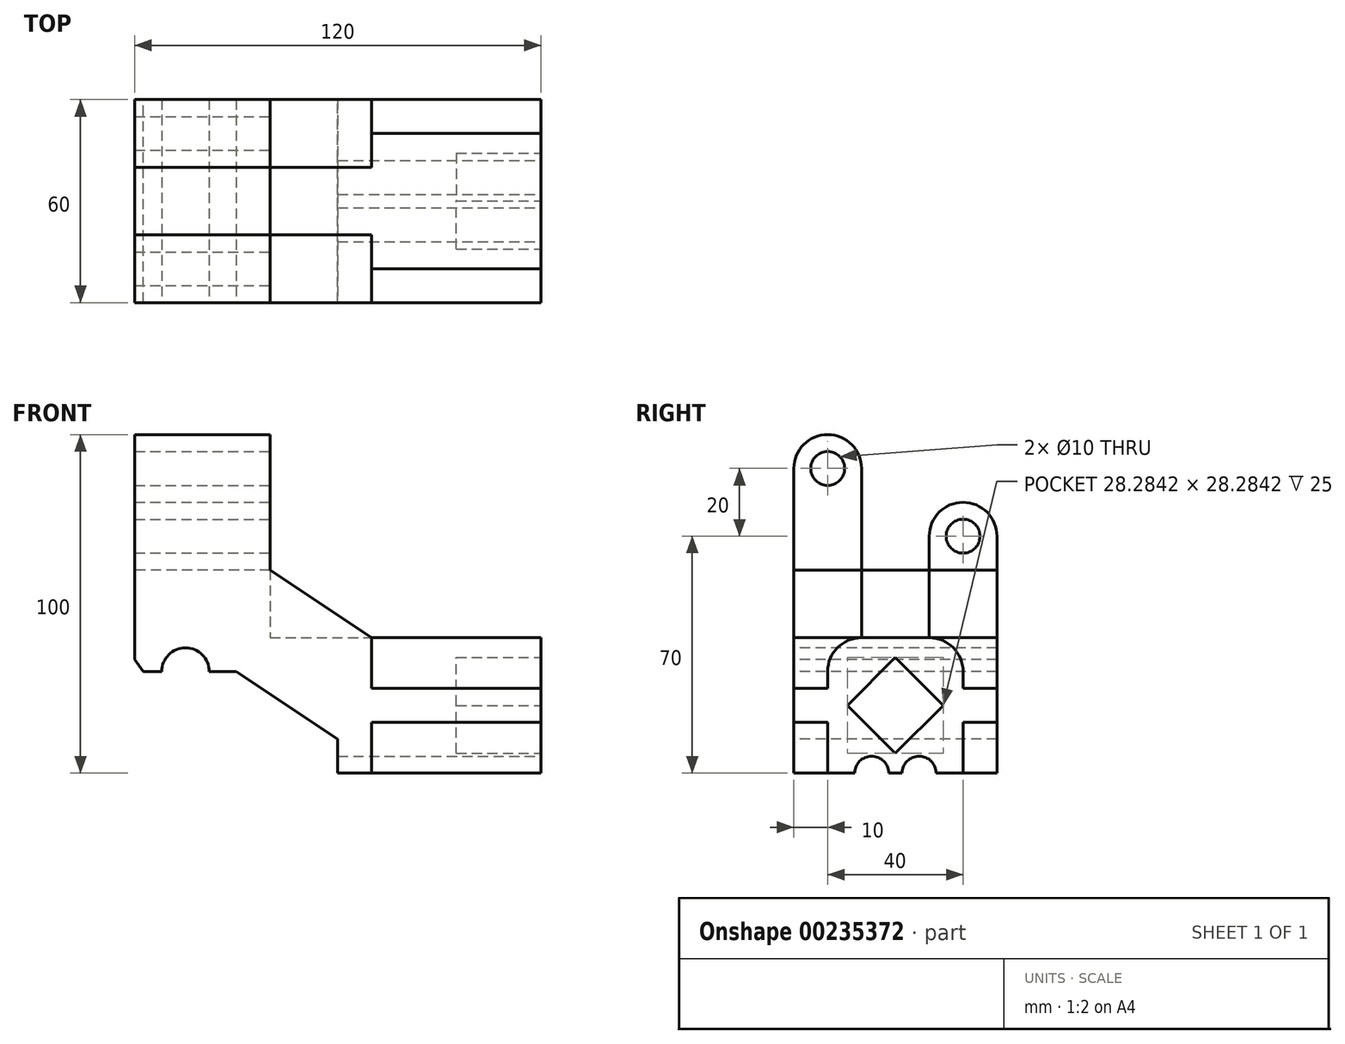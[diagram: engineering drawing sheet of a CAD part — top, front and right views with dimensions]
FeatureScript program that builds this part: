
annotation { "Feature Type Name" : "Feature", "Feature Type Description" : "" }
export const myFeature = defineFeature(function(context is Context, id is Id, definition is map)
    precondition{}
    {
        {
            var Q0;
            Q0=qCreatedBy(makeId("Front.planeOp"),FACE);
            var sketch = newSketch(context, id + "F0", { "sketchPlane" : qUnion([Q0])});
            skLineSegment(sketch, "E0", {"start": v(-120, 40) * mm, "end": v(-80, 40) * mm});
            skLineSegment(sketch, "E1", {"start": v(-80, 40) * mm, "end": v(-50, 20) * mm});
            skLineSegment(sketch, "E2", {"start": v(-50, 20) * mm, "end": v(-50, -20) * mm});
            skLineSegment(sketch, "E3", {"start": v(-50, -20) * mm, "end": v(-120, -20) * mm});
            skLineSegment(sketch, "E4", {"start": v(-120, -20) * mm, "end": v(-120, 40) * mm});
            skSolve(sketch);
        }
        {
            var Q0;
            Q0 = qSketchRegion(id + "F0", true);
            extrude(context, id + "F1", {"entities" : qUnion([Q0]), "depth" : 30 * mm, "hasSecondDirection" : true, "secondDirectionOppositeDirection" : true, "secondDirectionDepth" : 30 * mm});
        }
        {
            var Q0;
            Q0=makeQuery(id+"F1.opExtrude","CAP_FACE",FACE,{"disambiguationData":[OSD([sQuery(id+"F0.wireOp",EDGE,"E0"),sQuery(id+"F0.wireOp",EDGE,"E1"),sQuery(id+"F0.wireOp",EDGE,"E2"),sQuery(id+"F0.wireOp",EDGE,"E3"),sQuery(id+"F0.wireOp",EDGE,"E4")])],"isStart":false});
            var sketch = newSketch(context, id + "F2", { "sketchPlane" : qUnion([Q0])});
            skLineSegment(sketch, "E5", {"start": v(-128, 10) * mm, "end": v(-90, 10) * mm});
            skLineSegment(sketch, "E6", {"start": v(-90, 10) * mm, "end": v(-60, -10) * mm});
            skLineSegment(sketch, "E7", {"start": v(-60, -10) * mm, "end": v(-60, -28) * mm});
            skLineSegment(sketch, "E8", {"start": v(-60, -28) * mm, "end": v(-128, -28) * mm});
            skLineSegment(sketch, "E9", {"start": v(-128, -28) * mm, "end": v(-128, 10) * mm});
            skSolve(sketch);
        }
        {
            var Q0;
            Q0=makeQuery(id+"F1.opExtrude","SWEPT_FACE",FACE,{"disambiguationData":[OSD([sQuery(id+"F0.wireOp",EDGE,"E2")])]});
            var sketch = newSketch(context, id + "F3", { "sketchPlane" : qUnion([Q0])});
            skLineSegment(sketch, "E10.bottom", {"start": v(10, 48) * mm, "end": v(-10, 48) * mm});
            skLineSegment(sketch, "E10.top", {"start": v(10, -48) * mm, "end": v(-10, -48) * mm});
            skLineSegment(sketch, "E10.left", {"start": v(10, 48) * mm, "end": v(10, -48) * mm});
            skLineSegment(sketch, "E10.right", {"start": v(-10, 48) * mm, "end": v(-10, -48) * mm});
            skPoint(sketch, "E10.middle", {"position": v(0, 0) * mm});
            skSolve(sketch);
        }
        {
            var Q0;
            Q0 = qSketchRegion(id + "F3", true);
            extrude(context, id + "F4", {"entities" : qUnion([Q0]), "operationType" : NewBodyOperationType.REMOVE, "oppositeDirection" : true, "depth" : 30 * mm});
        }
        {
            var Q0;
            Q0=makeQuery(id+"F4.boolean.opBoolean","COPY",FACE,{"derivedFrom":makeQuery(id+"F4.opExtrude","CAP_FACE",FACE,{"disambiguationData":[OSD([sQuery(id+"F3.wireOp",EDGE,"E10.bottom"),sQuery(id+"F3.wireOp",EDGE,"E10.top"),sQuery(id+"F3.wireOp",EDGE,"E10.left"),sQuery(id+"F3.wireOp",EDGE,"E10.right")])],"isStart":false})});
            var sketch = newSketch(context, id + "F5", { "sketchPlane" : qUnion([Q0])});
            skLineSegment(sketch, "E11", {"start": v(-10, 20) * mm, "end": v(-10, 70) * mm});
            skLineSegment(sketch, "E12.0", {"start": v(-30, 20) * mm, "end": v(-30, 70) * mm});
            skLineSegment(sketch, "E13", {"start": v(-34.18, 80) * mm, "end": v(-4.8, 80) * mm, "construction": true});
            skArc(sketch, "E14", {"start": v(-10, 70) * mm, "mid": v(-20, 80) * mm, "end": v(-30, 70) * mm});
            skLineSegment(sketch, "E15", {"start": v(10, 20) * mm, "end": v(10, 50) * mm});
            skLineSegment(sketch, "E16.0", {"start": v(30, 20) * mm, "end": v(30, 50) * mm});
            skLineSegment(sketch, "E17", {"start": v(7.5, 60) * mm, "end": v(33.12, 60) * mm, "construction": true});
            skArc(sketch, "E18", {"start": v(30, 50) * mm, "mid": v(20, 60) * mm, "end": v(10, 50) * mm});
            skLineSegment(sketch, "E19", {"start": v(-30, 20) * mm, "end": v(-10, 20) * mm});
            skLineSegment(sketch, "E20", {"start": v(10, 20) * mm, "end": v(30, 20) * mm});
            skSolve(sketch);
        }
        {
            var Q0;
            Q0 = qSketchRegion(id + "F5", true);
            extrude(context, id + "F6", {"entities" : qUnion([Q0]), "operationType" : NewBodyOperationType.ADD, "oppositeDirection" : true, "depth" : 40 * mm});
        }
        {
            var Q0;
            Q0=qCreatedBy(makeId("Right.planeOp"),FACE);
            var sketch = newSketch(context, id + "F7", { "sketchPlane" : qUnion([Q0])});
            skLineSegment(sketch, "E21", {"start": v(-30, 5) * mm, "end": v(-20, 5) * mm});
            skLineSegment(sketch, "E22", {"start": v(-20, 5) * mm, "end": v(-20, 20) * mm});
            skLineSegment(sketch, "E23", {"start": v(-20, 20) * mm, "end": v(20, 20) * mm});
            skLineSegment(sketch, "E24", {"start": v(20, 20) * mm, "end": v(20, 5) * mm});
            skLineSegment(sketch, "E25", {"start": v(20, 5) * mm, "end": v(30, 5) * mm});
            skLineSegment(sketch, "E26", {"start": v(30, 5) * mm, "end": v(30, -5) * mm});
            skLineSegment(sketch, "E27", {"start": v(30, -5) * mm, "end": v(20, -5) * mm});
            skLineSegment(sketch, "E28", {"start": v(20, -5) * mm, "end": v(20, -20) * mm});
            skLineSegment(sketch, "E29", {"start": v(20, -20) * mm, "end": v(-20, -20) * mm});
            skLineSegment(sketch, "E30", {"start": v(-20, -20) * mm, "end": v(-20, -5) * mm});
            skLineSegment(sketch, "E31", {"start": v(-20, -5) * mm, "end": v(-30, -5) * mm});
            skLineSegment(sketch, "E32", {"start": v(-30, -5) * mm, "end": v(-30, 5) * mm});
            skSolve(sketch);
        }
        {
            var Q0;
            Q0 = qSketchRegion(id + "F7", true);
            extrude(context, id + "F8", {"entities" : qUnion([Q0]), "operationType" : NewBodyOperationType.ADD, "oppositeDirection" : true, "depth" : 90 * mm});
        }
        {
            var Q0;
            Q0 = qSketchRegion(id + "F2", true);
            extrude(context, id + "F9", {"entities" : qUnion([Q0]), "operationType" : NewBodyOperationType.REMOVE, "endBound" : BoundingType.THROUGH_ALL, "oppositeDirection" : true, "depth" : 25 * mm});
        }
        {
            var Q0;
            Q0=makeQuery(id+"F8.opExtrude","CAP_FACE",FACE,{"disambiguationData":[OSD([sQuery(id+"F7.wireOp",EDGE,"E21"),sQuery(id+"F7.wireOp",EDGE,"E22"),sQuery(id+"F7.wireOp",EDGE,"E23"),sQuery(id+"F7.wireOp",EDGE,"E24"),sQuery(id+"F7.wireOp",EDGE,"E25"),sQuery(id+"F7.wireOp",EDGE,"E26"),sQuery(id+"F7.wireOp",EDGE,"E27"),sQuery(id+"F7.wireOp",EDGE,"E28"),sQuery(id+"F7.wireOp",EDGE,"E29"),sQuery(id+"F7.wireOp",EDGE,"E30"),sQuery(id+"F7.wireOp",EDGE,"E31"),sQuery(id+"F7.wireOp",EDGE,"E32")])],"isStart":true});
            var sketch = newSketch(context, id + "F10", { "sketchPlane" : qUnion([Q0])});
            skCircle(sketch, "E33", {"center": v(0, 0) * mm, "radius": 10 * mm, "construction": true});
            skLineSegment(sketch, "E34", {"start": v(-14.14, 0) * mm, "end": v(0, 14.14) * mm});
            skLineSegment(sketch, "E35", {"start": v(0, 14.14) * mm, "end": v(14.14, 0) * mm});
            skLineSegment(sketch, "E36", {"start": v(14.14, 0) * mm, "end": v(0, -14.14) * mm});
            skLineSegment(sketch, "E37", {"start": v(0, -14.14) * mm, "end": v(-14.14, 0) * mm});
            skSolve(sketch);
        }
        {
            var Q0;
            Q0 = qSketchRegion(id + "F10", true);
            extrude(context, id + "F11", {"entities" : qUnion([Q0]), "operationType" : NewBodyOperationType.REMOVE, "oppositeDirection" : true, "depth" : 25 * mm});
        }
        {
            var Q0;
            Q0=makeQuery(id+"F8.opExtrude","SWEPT_EDGE",EDGE,{"disambiguationData":[OSD([sQuery(id+"F7.wireOp",EDGE,"E23"),sQuery(id+"F7.wireOp",EDGE,"E24")])]});
            var Q1;
            Q1=makeQuery(id+"F8.opExtrude","SWEPT_EDGE",EDGE,{"disambiguationData":[OSD([sQuery(id+"F7.wireOp",EDGE,"E22"),sQuery(id+"F7.wireOp",EDGE,"E23")])]});
            fillet(context, id + "F12", {"entities" : qUnion([Q0, Q1]), "radius" : 10 * mm, "tangentPropagation" : true, "allowEdgeOverflow" : false});
        }
        {
            var Q0;
            Q0=makeQuery(id+"F8.opExtrude","CAP_FACE",FACE,{"disambiguationData":[OSD([sQuery(id+"F7.wireOp",EDGE,"E21"),sQuery(id+"F7.wireOp",EDGE,"E22"),sQuery(id+"F7.wireOp",EDGE,"E23"),sQuery(id+"F7.wireOp",EDGE,"E24"),sQuery(id+"F7.wireOp",EDGE,"E25"),sQuery(id+"F7.wireOp",EDGE,"E26"),sQuery(id+"F7.wireOp",EDGE,"E27"),sQuery(id+"F7.wireOp",EDGE,"E28"),sQuery(id+"F7.wireOp",EDGE,"E29"),sQuery(id+"F7.wireOp",EDGE,"E30"),sQuery(id+"F7.wireOp",EDGE,"E31"),sQuery(id+"F7.wireOp",EDGE,"E32")])],"isStart":true});
            var sketch = newSketch(context, id + "F13", { "sketchPlane" : qUnion([Q0])});
            skLineSegment(sketch, "E38", {"start": v(-7, -15.84) * mm, "end": v(-7, -28.12) * mm, "construction": true});
            skCircle(sketch, "E39", {"center": v(-7, -20) * mm, "radius": 5 * mm});
            skCircle(sketch, "E40", {"center": v(7, -20) * mm, "radius": 5 * mm});
            skSolve(sketch);
        }
        {
            var Q0;
            Q0 = qSketchRegion(id + "F13", true);
            extrude(context, id + "F14", {"entities" : qUnion([Q0]), "operationType" : NewBodyOperationType.REMOVE, "endBound" : BoundingType.THROUGH_ALL, "oppositeDirection" : true, "depth" : 25 * mm});
        }
        {
            var Q0;
            Q0=makeQuery(id+"F6.opExtrude","CAP_FACE",FACE,{"disambiguationData":[OSD([sQuery(id+"F5.wireOp",EDGE,"E11"),sQuery(id+"F5.wireOp",EDGE,"E12.0"),sQuery(id+"F5.wireOp",EDGE,"E14"),sQuery(id+"F5.wireOp",EDGE,"E19")])],"isStart":true});
            var sketch = newSketch(context, id + "F15", { "sketchPlane" : qUnion([Q0])});
            skCircle(sketch, "E41", {"center": v(-20, 70) * mm, "radius": 5 * mm});
            skCircle(sketch, "E42", {"center": v(20, 50) * mm, "radius": 5 * mm});
            skSolve(sketch);
        }
        {
            var Q0;
            Q0 = qSketchRegion(id + "F15", true);
            extrude(context, id + "F16", {"entities" : qUnion([Q0]), "operationType" : NewBodyOperationType.REMOVE, "endBound" : BoundingType.THROUGH_ALL, "oppositeDirection" : true, "depth" : 25 * mm});
        }
        {
            var Q0;
            Q0=makeQuery(id+"F9.boolean.opBoolean","INTERSECT",EDGE,{"derivedFrom":[makeQuery(id+"F6.boolean.opBoolean","MERGE",FACE,{"derivedFrom":[makeQuery(id+"F1.opExtrude","SWEPT_FACE",FACE,{"disambiguationData":[OSD([sQuery(id+"F0.wireOp",EDGE,"E4")])]}),makeQuery(id+"F6.opExtrude","CAP_FACE",FACE,{"disambiguationData":[OSD([sQuery(id+"F5.wireOp",EDGE,"E11"),sQuery(id+"F5.wireOp",EDGE,"E12.0"),sQuery(id+"F5.wireOp",EDGE,"E14"),sQuery(id+"F5.wireOp",EDGE,"E19")])],"isStart":false}),makeQuery(id+"F6.opExtrude","CAP_FACE",FACE,{"disambiguationData":[OSD([sQuery(id+"F5.wireOp",EDGE,"E15"),sQuery(id+"F5.wireOp",EDGE,"E16.0"),sQuery(id+"F5.wireOp",EDGE,"E18"),sQuery(id+"F5.wireOp",EDGE,"E20")])],"isStart":false})]}),makeQuery(id+"F9.opExtrude","SWEPT_FACE",FACE,{"disambiguationData":[OSD([sQuery(id+"F2.wireOp",EDGE,"E5")])]})]});
            chamfer(context, id + "F17", {"entities" : qUnion([Q0]), "chamferType" : ChamferType.TWO_OFFSETS, "width1" : 3.5 * mm, "oppositeDirection" : false, "width2" : 2.5 * mm, "tangentPropagation" : true});
        }
        {
            var Q0;
            Q0=makeQuery(id+"F8.boolean.opBoolean","MERGE",FACE,{"derivedFrom":[makeQuery(id+"F6.boolean.opBoolean","MERGE",FACE,{"derivedFrom":[makeQuery(id+"F1.opExtrude","CAP_FACE",FACE,{"disambiguationData":[OSD([sQuery(id+"F0.wireOp",EDGE,"E0"),sQuery(id+"F0.wireOp",EDGE,"E1"),sQuery(id+"F0.wireOp",EDGE,"E2"),sQuery(id+"F0.wireOp",EDGE,"E3"),sQuery(id+"F0.wireOp",EDGE,"E4")])],"isStart":false}),makeQuery(id+"F6.opExtrude","SWEPT_FACE",FACE,{"disambiguationData":[OSD([sQuery(id+"F5.wireOp",EDGE,"E12.0")])]})]}),makeQuery(id+"F8.opExtrude","SWEPT_FACE",FACE,{"disambiguationData":[OSD([sQuery(id+"F7.wireOp",EDGE,"E32")])]})]});
            var sketch = newSketch(context, id + "F18", { "sketchPlane" : qUnion([Q0])});
            skCircle(sketch, "E43", {"center": v(-105, 10) * mm, "radius": 7 * mm});
            skSolve(sketch);
        }
        {
            var Q0;
            Q0 = qSketchRegion(id + "F18", true);
            extrude(context, id + "F19", {"entities" : qUnion([Q0]), "operationType" : NewBodyOperationType.REMOVE, "endBound" : BoundingType.THROUGH_ALL, "oppositeDirection" : true, "depth" : 25 * mm});
        }
    });
